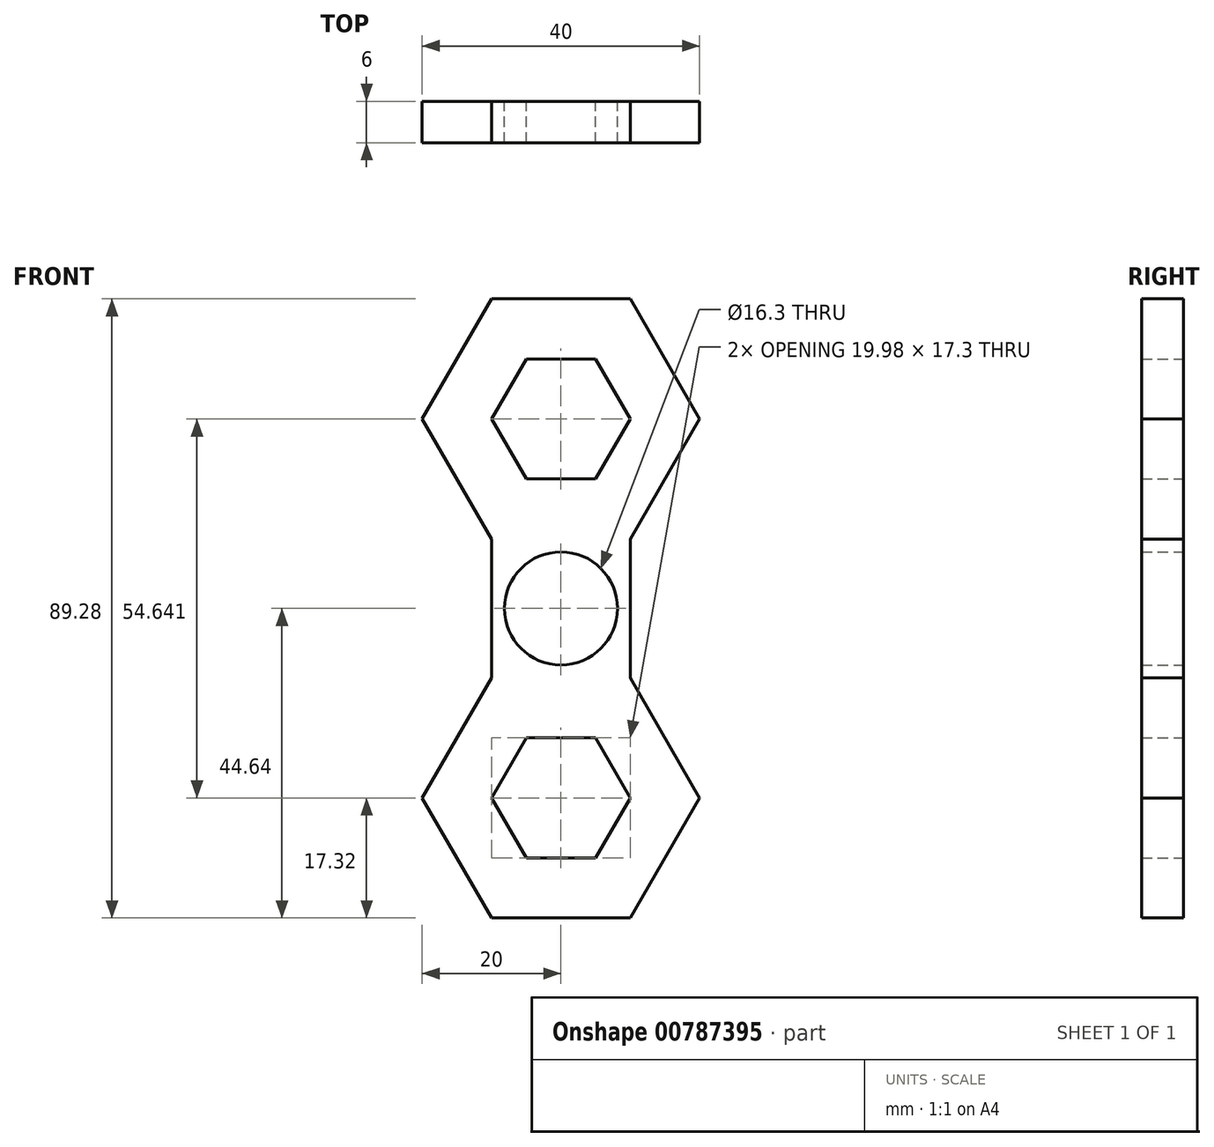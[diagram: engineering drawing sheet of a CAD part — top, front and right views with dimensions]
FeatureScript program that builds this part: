
annotation { "Feature Type Name" : "Feature", "Feature Type Description" : "" }
export const myFeature = defineFeature(function(context is Context, id is Id, definition is map)
    precondition{}
    {
        {
            var Q0;
            Q0=qCreatedBy(makeId("Front.planeOp"),FACE);
            var sketch = newSketch(context, id + "F0", { "sketchPlane" : qUnion([Q0])});
            skCircle(sketch, "E0", {"center": v(0, 0) * mm, "radius": 8.15 * mm});
            skLineSegment(sketch, "E1.bottom", {"start": v(10, -10) * mm, "end": v(-10, -10) * mm});
            skLineSegment(sketch, "E1.top", {"start": v(10, 10) * mm, "end": v(-10, 10) * mm});
            skLineSegment(sketch, "E1.left", {"start": v(10, -10) * mm, "end": v(10, 10) * mm});
            skLineSegment(sketch, "E1.right", {"start": v(-10, -10) * mm, "end": v(-10, 10) * mm});
            skPoint(sketch, "E2.0.midPoint", {"position": v(0, 10) * mm});
            skPoint(sketch, "E3.orphan", {"position": v(-22.47, 25.64) * mm});
            skPoint(sketch, "E4.orphan", {"position": v(-18.02, 45.14) * mm});
            skPoint(sketch, "E5.orphan", {"position": v(0, 53.81) * mm});
            skPoint(sketch, "E6.orphan", {"position": v(18.02, 45.14) * mm});
            skPoint(sketch, "E2.cCircle.center.orphan", {"position": v(0, 27.32) * mm});
            skPoint(sketch, "E7.orphan", {"position": v(-10, 10) * mm});
            skPoint(sketch, "E2.0.start.orphan", {"position": v(10, 10) * mm});
            skCircle(sketch, "E8.cCircle", {"center": v(0, 27.32) * mm, "radius": 17.32 * mm, "construction": true});
            skLineSegment(sketch, "E8.1", {"start": v(-10, 10) * mm, "end": v(-20, 27.32) * mm});
            skLineSegment(sketch, "E8.2", {"start": v(-20, 27.32) * mm, "end": v(-10, 44.64) * mm});
            skLineSegment(sketch, "E8.3", {"start": v(-10, 44.64) * mm, "end": v(10, 44.64) * mm});
            skLineSegment(sketch, "E8.4", {"start": v(10, 44.64) * mm, "end": v(20, 27.32) * mm});
            skLineSegment(sketch, "E8.5", {"start": v(20, 27.32) * mm, "end": v(10, 10) * mm});
            skLineSegment(sketch, "E9.MirrorCS", {"start": v(-20, -27.32) * mm, "end": v(-10, -44.64) * mm});
            skLineSegment(sketch, "E10.MirrorCS", {"start": v(-10, -10) * mm, "end": v(-20, -27.32) * mm});
            skLineSegment(sketch, "E11.MirrorCS", {"start": v(20, -27.32) * mm, "end": v(10, -10) * mm});
            skLineSegment(sketch, "E12.MirrorCS", {"start": v(10, -44.64) * mm, "end": v(20, -27.32) * mm});
            skLineSegment(sketch, "E13.MirrorCS", {"start": v(-10, -44.64) * mm, "end": v(10, -44.64) * mm});
            skCircle(sketch, "E14.cCircle", {"center": v(0, 27.32) * mm, "radius": 8.65 * mm, "construction": true});
            skLineSegment(sketch, "E14.0", {"start": v(9.99, 27.32) * mm, "end": v(5, 18.67) * mm});
            skLineSegment(sketch, "E14.1", {"start": v(5, 18.67) * mm, "end": v(-5, 18.67) * mm});
            skLineSegment(sketch, "E14.2", {"start": v(-5, 18.67) * mm, "end": v(-9.99, 27.32) * mm});
            skLineSegment(sketch, "E14.3", {"start": v(-9.99, 27.32) * mm, "end": v(-5, 35.97) * mm});
            skLineSegment(sketch, "E14.4", {"start": v(-5, 35.97) * mm, "end": v(5, 35.97) * mm});
            skLineSegment(sketch, "E14.5", {"start": v(5, 35.97) * mm, "end": v(9.99, 27.32) * mm});
            skPoint(sketch, "E14.0.midPoint", {"position": v(7.5, 23) * mm});
            skLineSegment(sketch, "E15.MirrorCS", {"start": v(-5, -35.97) * mm, "end": v(5, -35.97) * mm});
            skLineSegment(sketch, "E16.MirrorCS", {"start": v(-9.99, -27.32) * mm, "end": v(-5, -35.97) * mm});
            skLineSegment(sketch, "E17.MirrorCS", {"start": v(-5, -18.67) * mm, "end": v(-9.99, -27.32) * mm});
            skLineSegment(sketch, "E18.MirrorCS", {"start": v(5, -18.67) * mm, "end": v(-5, -18.67) * mm});
            skLineSegment(sketch, "E19.MirrorCS", {"start": v(9.99, -27.32) * mm, "end": v(5, -18.67) * mm});
            skLineSegment(sketch, "E20.MirrorCS", {"start": v(5, -35.97) * mm, "end": v(9.99, -27.32) * mm});
            skSolve(sketch);
        }
        {
            var Q0;
            Q0=makeQuery(id+"F0.imprint","IMPRINT",FACE,{"disambiguationData":[TD([[makeQuery(id+"F0.imprint","IMPRINT",EDGE,{"derivedFrom":sQuery(id+"F0.wireOp",EDGE,"E1.top")}),-1.0]])]});
            var Q1;
            Q1=makeQuery(id+"F0.imprint","IMPRINT",FACE,{"disambiguationData":[TD([[makeQuery(id+"F0.imprint","IMPRINT",EDGE,{"derivedFrom":sQuery(id+"F0.wireOp",EDGE,"E0")}),-1.0]])]});
            var Q2;
            Q2=makeQuery(id+"F0.imprint","IMPRINT",FACE,{"disambiguationData":[TD([[makeQuery(id+"F0.imprint","IMPRINT",EDGE,{"derivedFrom":sQuery(id+"F0.wireOp",EDGE,"E1.bottom")}),1.0]])]});
            extrude(context, id + "F1", {"entities" : qUnion([Q0, Q1, Q2]), "depth" : 6 * mm, "offsetDistance" : 25 * mm});
        }
    });
